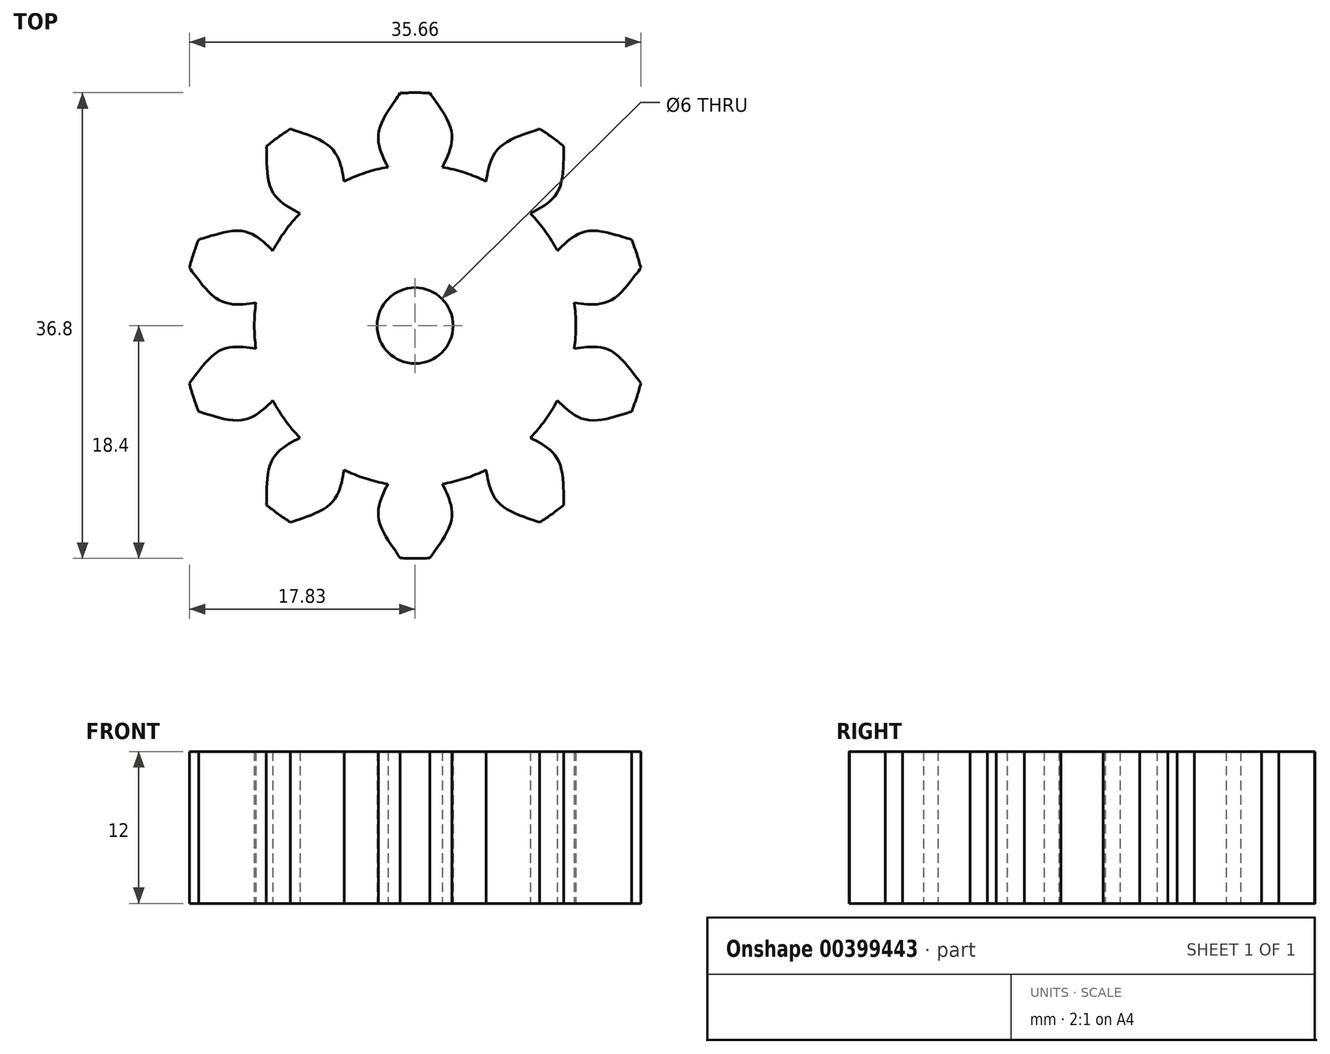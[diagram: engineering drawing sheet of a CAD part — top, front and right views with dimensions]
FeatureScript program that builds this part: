
annotation { "Feature Type Name" : "Feature", "Feature Type Description" : "" }
export const myFeature = defineFeature(function(context is Context, id is Id, definition is map)
    precondition{}
    {
        {
            var Q0;
            Q0=qCreatedBy(makeId("Top.planeOp"),FACE);
            var sketch = newSketch(context, id + "F0", { "sketchPlane" : qUnion([Q0])});
            skCircle(sketch, "E0", {"center": v(0, 0) * mm, "radius": 18.4 * mm, "construction": true});
            skCircle(sketch, "E1", {"center": v(0, 0) * mm, "radius": 15.9 * mm, "construction": true});
            skCircle(sketch, "E2", {"center": v(0, 0) * mm, "radius": 12.7 * mm, "construction": true});
            skCircle(sketch, "E3", {"center": v(0, 0) * mm, "radius": 14.4 * mm, "construction": true});
            skLineSegment(sketch, "E4", {"start": v(0, 0) * mm, "end": v(2.49, 15.7) * mm, "construction": true});
            skFitSpline(sketch, "E5", {"points": [v(1.18, 18.36) * mm, v(2.49, 15.7) * mm, v(2.15, 12.52) * mm], "startDerivative": vector(2.76, -3.96) * mm, "endDerivative": vector(-3.39, -7.65) * mm});
            skLineSegment(sketch, "E6", {"start": v(-8.23, 11.82) * mm, "end": v(1.18, 18.36) * mm, "construction": true});
            skLineSegment(sketch, "E7", {"start": v(-6.44, 12.88) * mm, "end": v(1.94, 17.07) * mm, "construction": true});
            skLineSegment(sketch, "E8", {"start": v(-4, 13.84) * mm, "end": v(2.49, 15.7) * mm, "construction": true});
            skLineSegment(sketch, "E9", {"start": v(1.38, 14.33) * mm, "end": v(2.64, 14.21) * mm, "construction": true});
            skLineSegment(sketch, "E10", {"start": v(1.12, 18.44) * mm, "end": v(1.23, 18.28) * mm, "construction": true});
            skLineSegment(sketch, "E11", {"start": v(1.9, 17.16) * mm, "end": v(1.98, 16.98) * mm, "construction": true});
            skLineSegment(sketch, "E12", {"start": v(2.46, 15.8) * mm, "end": v(2.52, 15.6) * mm, "construction": true});
            skLineSegment(sketch, "E13", {"start": v(2.65, 14.31) * mm, "end": v(2.63, 14.11) * mm, "construction": true});
            skSolve(sketch);
        }
        {
            var Q0;
            Q0=qCreatedBy(makeId("Top.planeOp"),FACE);
            var sketch = newSketch(context, id + "F1", { "sketchPlane" : qUnion([Q0])});
            skFitSpline(sketch, "E14.0", {"points": [v(1.18, 18.36) * mm, v(1.63, 17.72) * mm, v(2.82, 15.57) * mm, v(2.73, 13.82) * mm, v(2.15, 12.52) * mm]});
            skFitSpline(sketch, "E15.MirrorCS", {"points": [v(-1.18, 18.36) * mm, v(-1.63, 17.72) * mm, v(-2.82, 15.57) * mm, v(-2.73, 13.82) * mm, v(-2.15, 12.52) * mm]});
            skArc(sketch, "E16", {"start": v(2.15, 12.52) * mm, "mid": v(0, -12.7) * mm, "end": v(-2.15, 12.52) * mm});
            skArc(sketch, "E17", {"start": v(1.18, 18.36) * mm, "mid": v(0, 18.4) * mm, "end": v(-1.18, 18.36) * mm});
            skCircle(sketch, "E18", {"center": v(0, 0) * mm, "radius": 3 * mm});
            skSolve(sketch);
        }
        {
            var Q0;
            Q0 = qSketchRegion(id + "F1", true);
            extrude(context, id + "F2", {"entities" : qUnion([Q0]), "depth" : 12 * mm});
        }
        {
            var Q0;
            Q0=makeQuery(id+"F2.opExtrude","SWEPT_BODY",BODY,{"disambiguationData":[OSD([sQuery(id+"F1.wireOp",EDGE,"E14.0"),sQuery(id+"F1.wireOp",EDGE,"E15.MirrorCS"),sQuery(id+"F1.wireOp",EDGE,"E16"),sQuery(id+"F1.wireOp",EDGE,"E17"),sQuery(id+"F1.wireOp",EDGE,"E18")])]});
            var Q1;
            Q1=makeQuery(id+"F2.opExtrude","SWEPT_FACE",FACE,{"disambiguationData":[OSD([sQuery(id+"F1.wireOp",EDGE,"E18")])]});
            circularPattern(context, id + "F3", {"operationType" : NewBodyOperationType.ADD, "entities" : qUnion([Q0]), "axis" : qUnion([Q1]), "angle" : 360 * degree, "instanceCount" : 10, "equalSpace" : true});
        }
    });
